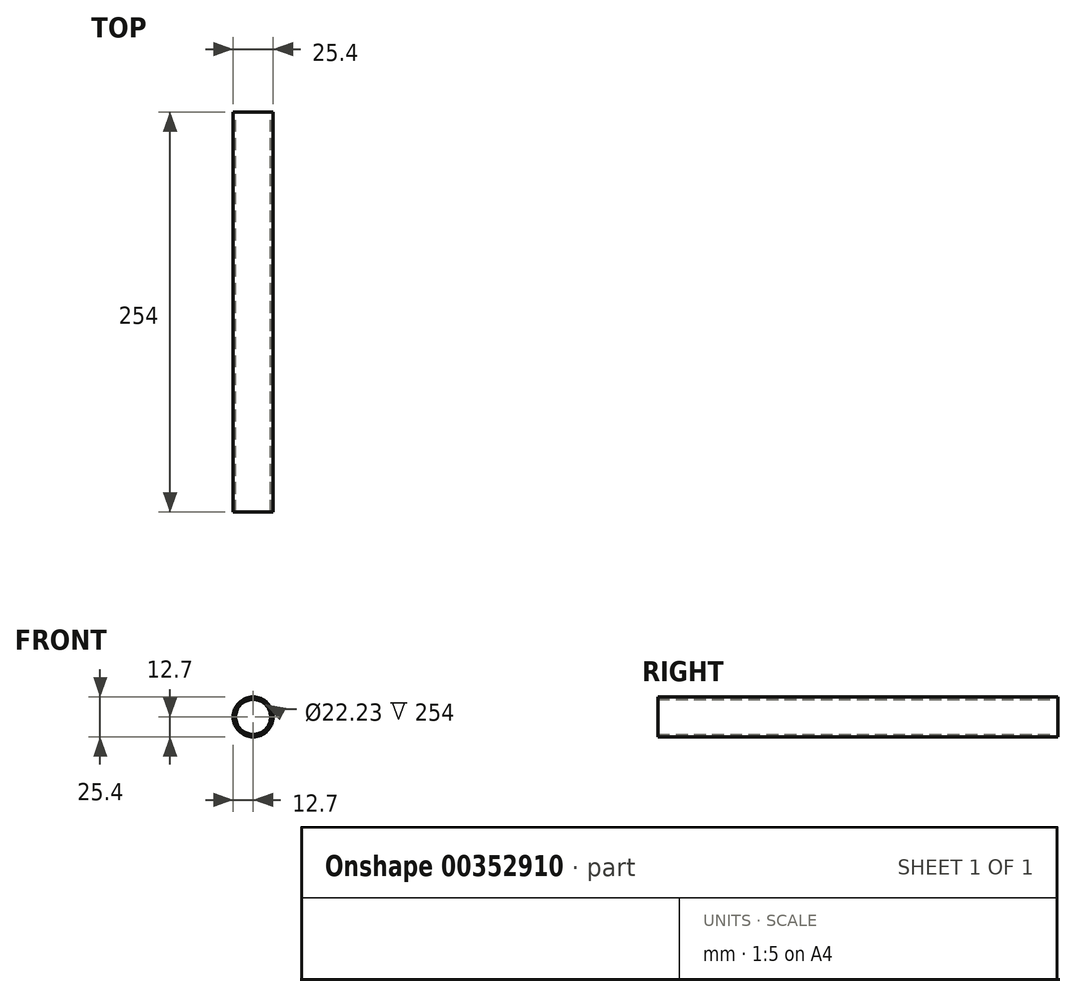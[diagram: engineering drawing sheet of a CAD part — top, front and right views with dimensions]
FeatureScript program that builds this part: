
annotation { "Feature Type Name" : "Feature", "Feature Type Description" : "" }
export const myFeature = defineFeature(function(context is Context, id is Id, definition is map)
    precondition{}
    {
        {
            var Q0;
            Q0=qCreatedBy(makeId("Front.planeOp"),FACE);
            var sketch = newSketch(context, id + "F0", { "sketchPlane" : qUnion([Q0])});
            skCircle(sketch, "E0", {"center": v(0, 0) * mm, "radius": 12.7 * mm});
            skCircle(sketch, "E1", {"center": v(0, 0) * mm, "radius": 11.11 * mm});
            skSolve(sketch);
        }
        {
            var Q0;
            Q0=qSketchRegion(id+"F0",true);
            extrude(context, id + "F1", {"entities" : qUnion([Q0]), "depth" : 254 * mm});
        }
    });
